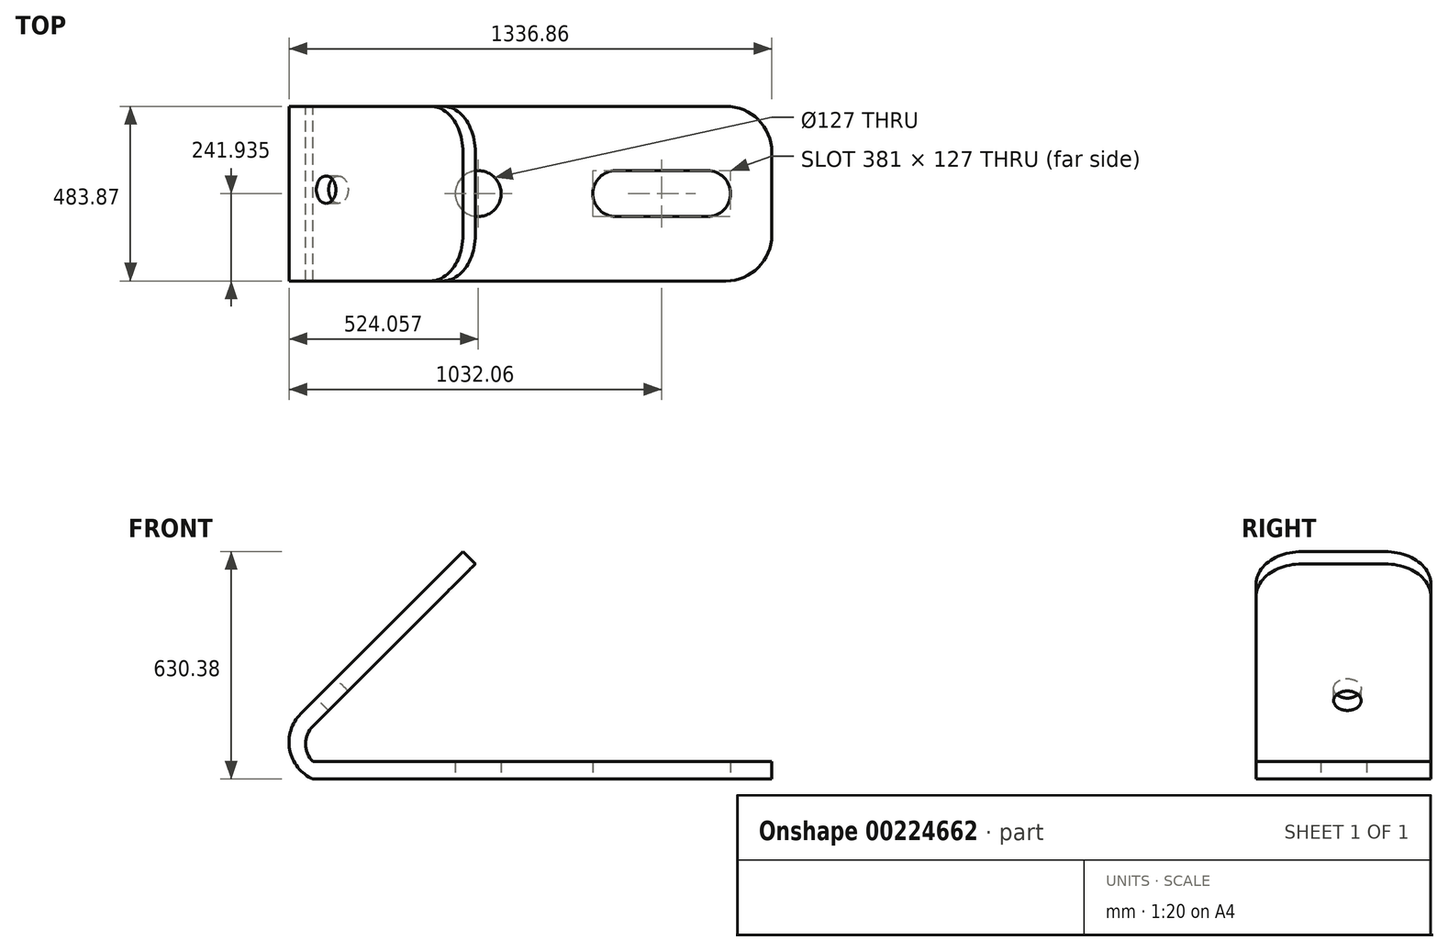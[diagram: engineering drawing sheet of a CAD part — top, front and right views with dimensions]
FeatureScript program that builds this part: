
annotation { "Feature Type Name" : "Feature", "Feature Type Description" : "" }
export const myFeature = defineFeature(function(context is Context, id is Id, definition is map)
    precondition{}
    {
        {
            var Q0;
            Q0=qCreatedBy(makeId("Front.planeOp"),FACE);
            var sketch = newSketch(context, id + "F0", { "sketchPlane" : qUnion([Q0])});
            skLineSegment(sketch, "E0", {"start": v(-449.01, 0) * mm, "end": v(820.99, 0) * mm});
            skLineSegment(sketch, "E1", {"start": v(820.99, 0) * mm, "end": v(820.99, 48.26) * mm});
            skLineSegment(sketch, "E2", {"start": v(820.99, 48.26) * mm, "end": v(-449.01, 48.26) * mm});
            skLineSegment(sketch, "E3", {"start": v(0, 596.26) * mm, "end": v(-449.01, 147.24) * mm});
            skLineSegment(sketch, "E4", {"start": v(0, 596.26) * mm, "end": v(-34.12, 630.38) * mm});
            skLineSegment(sketch, "E5", {"start": v(-34.12, 630.38) * mm, "end": v(-483.14, 181.37) * mm});
            skArc(sketch, "E6", {"start": v(-483.14, 181.37) * mm, "mid": v(-513.94, 81.68) * mm, "end": v(-449.01, 0) * mm});
            skArc(sketch, "E7", {"start": v(-449.01, 147.24) * mm, "mid": v(-469.51, 97.75) * mm, "end": v(-449.01, 48.26) * mm});
            skSolve(sketch);
        }
        {
            var Q0;
            Q0 = qSketchRegion(id + "F0", true);
            extrude(context, id + "F1", {"entities" : qUnion([Q0]), "depth" : 483.87 * mm});
        }
        {
            var Q0;
            Q0=makeQuery(id+"F1.opExtrude","SWEPT_FACE",FACE,{"disambiguationData":[OSD([sQuery(id+"F0.wireOp",EDGE,"E0")])]});
            var sketch = newSketch(context, id + "F2", { "sketchPlane" : qUnion([Q0])});
            skLineSegment(sketch, "E8", {"start": v(-449.01, 241.94) * mm, "end": v(820.99, 241.94) * mm, "construction": true});
            skCircle(sketch, "E9", {"center": v(8.19, 241.93) * mm, "radius": 63.5 * mm});
            skCircle(sketch, "E10", {"center": v(389.19, 241.94) * mm, "radius": 63.5 * mm});
            skCircle(sketch, "E11", {"center": v(643.19, 241.94) * mm, "radius": 63.5 * mm});
            skLineSegment(sketch, "E12", {"start": v(389.19, 305.44) * mm, "end": v(643.19, 305.44) * mm});
            skLineSegment(sketch, "E13", {"start": v(389.19, 178.44) * mm, "end": v(643.19, 178.44) * mm});
            skSolve(sketch);
        }
        {
            var Q0;
            Q0 = qSketchRegion(id + "F2", true);
            extrude(context, id + "F3", {"entities" : qUnion([Q0]), "operationType" : NewBodyOperationType.REMOVE, "oppositeDirection" : true, "depth" : 142.24 * mm});
        }
        {
            var Q0;
            Q0=makeQuery(id+"F1.opExtrude","SWEPT_FACE",FACE,{"disambiguationData":[OSD([sQuery(id+"F0.wireOp",EDGE,"E5")])]});
            var sketch = newSketch(context, id + "F4", { "sketchPlane" : qUnion([Q0])});
            skCircle(sketch, "E14", {"center": v(231.12, -114.3) * mm, "radius": 38.1 * mm});
            skCircle(sketch, "E15", {"center": v(231.12, -369.57) * mm, "radius": 38.1 * mm});
            skSolve(sketch);
        }
        {
            var Q0;
            Q0 = qSketchRegion(id + "F4", true);
            extrude(context, id + "F5", {"entities" : qUnion([Q0]), "operationType" : NewBodyOperationType.REMOVE, "oppositeDirection" : true, "depth" : 73.66 * mm});
        }
        {
            var Q0;
            Q0=makeQuery(id+"F1.opExtrude","CAP_EDGE",EDGE,{"disambiguationData":[OSD([sQuery(id+"F0.wireOp",EDGE,"E4")])],"isStart":false});
            fillet(context, id + "F6", {"entities" : qUnion([Q0]), "radius" : 127 * mm, "tangentPropagation" : true, "allowEdgeOverflow" : false});
        }
        {
            var Q0;
            Q0=makeQuery(id+"F1.opExtrude","CAP_EDGE",EDGE,{"disambiguationData":[OSD([sQuery(id+"F0.wireOp",EDGE,"E4")])],"isStart":true});
            fillet(context, id + "F7", {"entities" : qUnion([Q0]), "radius" : 127 * mm, "tangentPropagation" : true, "allowEdgeOverflow" : false});
        }
        {
            var Q0;
            Q0=makeQuery(id+"F1.opExtrude","CAP_EDGE",EDGE,{"disambiguationData":[OSD([sQuery(id+"F0.wireOp",EDGE,"E1")])],"isStart":false});
            fillet(context, id + "F8", {"entities" : qUnion([Q0]), "radius" : 127 * mm, "tangentPropagation" : true, "allowEdgeOverflow" : false});
        }
        {
            var Q0;
            Q0=makeQuery(id+"F1.opExtrude","CAP_EDGE",EDGE,{"disambiguationData":[OSD([sQuery(id+"F0.wireOp",EDGE,"E1")])],"isStart":true});
            fillet(context, id + "F9", {"entities" : qUnion([Q0]), "radius" : 127 * mm, "tangentPropagation" : true, "allowEdgeOverflow" : false});
        }
    });
